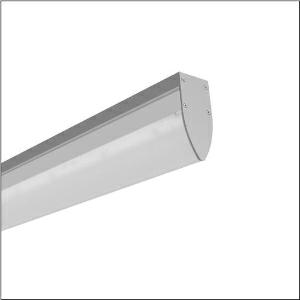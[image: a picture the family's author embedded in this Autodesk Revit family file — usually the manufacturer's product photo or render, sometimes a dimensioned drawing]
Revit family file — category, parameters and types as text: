
# Revit family: mira_r__21_td_51fr527k474a_9fa0
name_source: partatom
category: Lighting Fixtures
units: mm (PartAtom-declared; Revit-internal decimal feet)

## family parameters
Cut with Voids When Loaded = No
Host = Face
Light Source = No
Part Type = Normal
Room Calculation Point = No
Round Connector Dimension = Use Diameter
Shared = No

## types (1)
- Mira® 21 TD (1 x LED, 7330 lm, 52 W, 4000K)
    Apparent Load = 52 VA
    CIE Flux Codes = 40 68 87 81 100
    Color Rendering = 80
    Color Temperature = 4000K
    Default Elevation = 1800 mm
    Description = Mira® 21 TD, clean room luminaire, primary light control with reflector, primary optical cover: cover, of PMMA, frosted, light emission: direct distribution, primary light characteristic: symmetric, installation type: surface-mounted, LED, rated luminous flux: 7.330lm, luminous efficacy: 141lm/W, light colour: 840, colour temperature: 4000K, control gear: ECG, with terminal, 3-pole, max. 2.5mm², mains connection: 230V, AC, 50/60Hz, rated input power: 52W, luminaire housing, of sheet steel, coated, pure white (RAL 9010), length: 1.200mm, width: 55mm, height: 120mm, protection rating (complete): IP43, insulation class (complete): insulation class I (protective earthing), certification: CE, UKCA, permissible operating ambient temperature: -5..+40°C, standard: EN 50419, packaging unit: 1 piece
    Height = 0 mm  [stored 0 ft]
    Lamp = 1 x LED
    Lamp Light Flux = 7330 lm
    Lamp Power = 52 W
    Lamp count = 1
    Length = 1200 mm
    Luminous efficacy = 141 lm/W
    Manufacturer = Siteco
    ModVariant = No
    Model = 51FR527K474A
    Mounting Place = Ceiling
    Mounting Type = Recessed
    Number of Poles = 1
    OnlyDefault = Yes
    Power Factor = 1
    Product Name = Mira® 21 TD
    Product group = clean room luminaire
    ProductGroupID = 402
    Protection Class = Protection class I
    Protection Degree = IP 43
    RLX_Detail_Level = 1
    RLX_Emergency_Light_Flux = 0 lm
    RLX_Emergency_Type = 0
    RLX_Emergency_Type_DB = No
    RlxData = <blob elided: 25153 chars, md5=a1f206f9>
    Socket = socket
    Standby Power = 0 W
    System Light Flux = 7330 lm
    System Power = 52 W
    Type Comments = Product without accessories
    Type Image = l_1007115.jpg
    URL = http://relux.com
    VarID = ---
    Voltage = 0 V
    Weight = 0.00 kg
    Width = 55 mm

note: [stored X ft] marks values corroborated as IEEE doubles in the binary element streams (Revit-internal decimal feet)

## geometry (parser evidence)
native form markers: Blend x4, Sweep x12
no freeform markers — native parametric forms only
